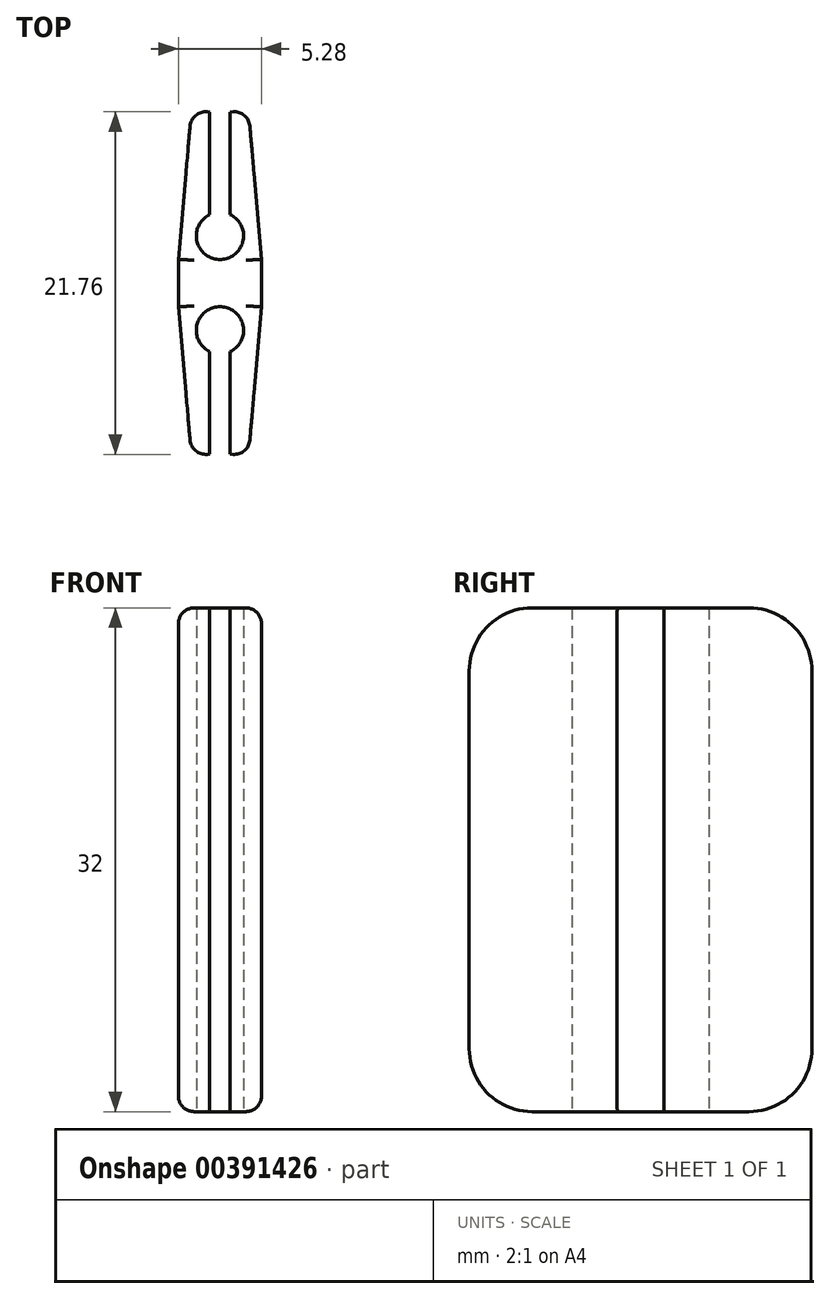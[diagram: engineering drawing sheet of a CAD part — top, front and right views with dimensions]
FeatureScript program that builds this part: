
annotation { "Feature Type Name" : "Feature", "Feature Type Description" : "" }
export const myFeature = defineFeature(function(context is Context, id is Id, definition is map)
    precondition{}
    {
        {
            var Q0;
            Q0=qCreatedBy(makeId("Top.planeOp"),FACE);
            var sketch = newSketch(context, id + "F0", { "sketchPlane" : qUnion([Q0])});
            skLineSegment(sketch, "E0", {"start": v(-2.64, -1.5) * mm, "end": v(-1.81, -10.96) * mm});
            skCircle(sketch, "E1", {"center": v(0, -3) * mm, "radius": 1.5 * mm});
            skLineSegment(sketch, "E2", {"start": v(-1.81, -10.96) * mm, "end": v(-0.65, -10.86) * mm});
            skLineSegment(sketch, "E3", {"start": v(-0.65, -10.86) * mm, "end": v(-0.65, -4.35) * mm});
            skLineSegment(sketch, "E4", {"start": v(0, -3) * mm, "end": v(0, -45.93) * mm, "construction": true});
            skLineSegment(sketch, "E5", {"start": v(-2.64, -1.5) * mm, "end": v(0, -1.5) * mm});
            skLineSegment(sketch, "E6.MirrorCS", {"start": v(2.64, -1.5) * mm, "end": v(0, -1.5) * mm});
            skLineSegment(sketch, "E7.MirrorCS", {"start": v(2.64, -1.5) * mm, "end": v(1.81, -10.96) * mm});
            skLineSegment(sketch, "E8.MirrorCS", {"start": v(0.65, -10.86) * mm, "end": v(0.65, -4.35) * mm});
            skLineSegment(sketch, "E9.MirrorCS", {"start": v(1.81, -10.96) * mm, "end": v(0.65, -10.86) * mm});
            skLineSegment(sketch, "E10", {"start": v(-5.05, 0) * mm, "end": v(5.33, 0) * mm, "construction": true});
            skLineSegment(sketch, "E11.MirrorCS", {"start": v(-2.64, 1.5) * mm, "end": v(0, 1.5) * mm});
            skLineSegment(sketch, "E12.MirrorCS", {"start": v(2.64, 1.5) * mm, "end": v(0, 1.5) * mm});
            skLineSegment(sketch, "E13.MirrorCS", {"start": v(-2.64, 1.5) * mm, "end": v(-1.81, 10.96) * mm});
            skCircle(sketch, "E14.MirrorC", {"center": v(0, 3) * mm, "radius": 1.5 * mm});
            skLineSegment(sketch, "E15.MirrorCS", {"start": v(-0.65, 10.86) * mm, "end": v(-0.65, 4.35) * mm});
            skLineSegment(sketch, "E16.MirrorCS", {"start": v(-1.81, 10.96) * mm, "end": v(-0.65, 10.86) * mm});
            skLineSegment(sketch, "E17.MirrorCS", {"start": v(1.81, 10.96) * mm, "end": v(0.65, 10.86) * mm});
            skLineSegment(sketch, "E18.MirrorCS", {"start": v(0.65, 10.86) * mm, "end": v(0.65, 4.35) * mm});
            skLineSegment(sketch, "E19.MirrorCS", {"start": v(2.64, 1.5) * mm, "end": v(1.81, 10.96) * mm});
            skLineSegment(sketch, "E20", {"start": v(-2.64, 1.5) * mm, "end": v(-2.64, -1.5) * mm});
            skLineSegment(sketch, "E21", {"start": v(2.64, 1.5) * mm, "end": v(2.64, -1.5) * mm});
            skSolve(sketch);
        }
        {
            var Q0;
            Q0=makeQuery(id+"F0.imprint","IMPRINT",FACE,{"disambiguationData":[TD([[makeQuery(id+"F0.imprint","IMPRINT",EDGE,{"derivedFrom":sQuery(id+"F0.wireOp",EDGE,"E0")}),1.0]])]});
            var Q1;
            Q1=makeQuery(id+"F0.imprint","IMPRINT",FACE,{"disambiguationData":[TD([[makeQuery(id+"F0.imprint","IMPRINT",EDGE,{"derivedFrom":sQuery(id+"F0.wireOp",EDGE,"E5")}),1.0]])]});
            var Q2;
            Q2=makeQuery(id+"F0.imprint","IMPRINT",FACE,{"disambiguationData":[TD([[makeQuery(id+"F0.imprint","IMPRINT",EDGE,{"derivedFrom":sQuery(id+"F0.wireOp",EDGE,"E11.MirrorCS")}),1.0]])]});
            var Q3;
            {var subQ2=sQuery(id+"F0.wireOp",EDGE,"E12.MirrorCS");Q3=makeQuery(id+"F0.imprint","IMPRINT",FACE,{"disambiguationData":[TD([[makeQuery(id+"F0.imprint","IMPRINT",EDGE,{"derivedFrom":subQ2}),-1.0]])]});}
            var Q4;
            {var subQ1=sQuery(id+"F0.wireOp",EDGE,"E6.MirrorCS");Q4=makeQuery(id+"F0.imprint","IMPRINT",FACE,{"disambiguationData":[TD([[makeQuery(id+"F0.imprint","IMPRINT",EDGE,{"derivedFrom":subQ1}),1.0]])]});}
            extrude(context, id + "F1", {"entities" : qUnion([Q0, Q1, Q2, Q3, Q4]), "depth" : 32 * mm});
        }
        {
            var Q0;
            Q0=makeQuery(id+"F1.opExtrude","CAP_EDGE",EDGE,{"disambiguationData":[OSD([sQuery(id+"F0.wireOp",EDGE,"E2")])],"isStart":false});
            var Q1;
            Q1=makeQuery(id+"F1.opExtrude","CAP_EDGE",EDGE,{"disambiguationData":[OSD([sQuery(id+"F0.wireOp",EDGE,"E9.MirrorCS")])],"isStart":false});
            var Q2;
            Q2=makeQuery(id+"F1.opExtrude","CAP_EDGE",EDGE,{"disambiguationData":[OSD([sQuery(id+"F0.wireOp",EDGE,"E2")])],"isStart":true});
            var Q3;
            Q3=makeQuery(id+"F1.opExtrude","CAP_EDGE",EDGE,{"disambiguationData":[OSD([sQuery(id+"F0.wireOp",EDGE,"E9.MirrorCS")])],"isStart":true});
            var Q4;
            Q4=makeQuery(id+"F1.opExtrude","CAP_EDGE",EDGE,{"disambiguationData":[OSD([sQuery(id+"F0.wireOp",EDGE,"E16.MirrorCS")])],"isStart":false});
            var Q5;
            Q5=makeQuery(id+"F1.opExtrude","CAP_EDGE",EDGE,{"disambiguationData":[OSD([sQuery(id+"F0.wireOp",EDGE,"E17.MirrorCS")])],"isStart":false});
            var Q6;
            Q6=makeQuery(id+"F1.opExtrude","CAP_EDGE",EDGE,{"disambiguationData":[OSD([sQuery(id+"F0.wireOp",EDGE,"E16.MirrorCS")])],"isStart":true});
            var Q7;
            Q7=makeQuery(id+"F1.opExtrude","CAP_EDGE",EDGE,{"disambiguationData":[OSD([sQuery(id+"F0.wireOp",EDGE,"E17.MirrorCS")])],"isStart":true});
            fillet(context, id + "F2", {"entities" : qUnion([Q0, Q1, Q2, Q3, Q4, Q5, Q6, Q7]), "radius" : 4 * mm, "tangentPropagation" : true, "allowEdgeOverflow" : false});
        }
        {
            var Q0;
            Q0=makeQuery(id+"F1.opExtrude","SWEPT_EDGE",EDGE,{"disambiguationData":[OSD([sQuery(id+"F0.wireOp",EDGE,"E7.MirrorCS"),sQuery(id+"F0.wireOp",EDGE,"E9.MirrorCS")])]});
            var Q1;
            Q1=makeQuery(id+"F1.opExtrude","SWEPT_EDGE",EDGE,{"disambiguationData":[OSD([sQuery(id+"F0.wireOp",EDGE,"E0"),sQuery(id+"F0.wireOp",EDGE,"E2")])]});
            var Q2;
            Q2=makeQuery(id+"F1.opExtrude","SWEPT_EDGE",EDGE,{"disambiguationData":[OSD([sQuery(id+"F0.wireOp",EDGE,"E17.MirrorCS"),sQuery(id+"F0.wireOp",EDGE,"E19.MirrorCS")])]});
            var Q3;
            Q3=makeQuery(id+"F1.opExtrude","SWEPT_EDGE",EDGE,{"disambiguationData":[OSD([sQuery(id+"F0.wireOp",EDGE,"E13.MirrorCS"),sQuery(id+"F0.wireOp",EDGE,"E16.MirrorCS")])]});
            fillet(context, id + "F3", {"entities" : qUnion([Q0, Q1, Q2, Q3]), "radius" : 1 * mm, "tangentPropagation" : true, "allowEdgeOverflow" : false});
        }
    });
